# Revit family: svetilnik_alfresco_bourdon
name_source: partatom
category: Lighting Fixtures
revit_build: Autodesk Revit 2016 (Build: 20150506_1715(x64)
units: mm (PartAtom-declared; Revit-internal decimal feet)

## family parameters
Always vertical = Yes
Cut with Voids When Loaded = No
Light Source = Yes
Part Type = Normal
Room Calculation Point = No
Round Connector Dimension = Use Diameter
Shared = No
Work Plane-Based = No

## types (2) — shared parameters
ADSK_Единица измерения = шт.
ADSK_Завод-изготовитель = ALFRESCO
ADSK_Количество фаз = 2
ADSK_Количество фаз числовое = 2
ADSK_Коэффициент мощности = 0.98
ADSK_Масса = 36
ADSK_Напряжение = 220 V
ADSK_Номинальная мощность = 70 W
ADSK_Полная мощность = 71 VA
ADSK_Размер_Высота = 4175 mm  [stored 13.6975 ft]
ADSK_Размер_Диаметр = 300 mm
ADSK_Размер_Длина = 652 mm  [stored 2.13911 ft]
ADSK_Ток = 0 A
ADSK_Энергоэффективность = 90 lm/W
Apparent Load = 71 VA
Color Filter = 16777215
Dimming Lamp Color Temperature Shift = <None>
Emit from Line Length = 80 mm  [stored 0.262467 ft]
IP Class = IP 54
Manufacturer = ALFRESCO
Photometric Web File = Боурдон_70Вт_ДНаТ.ies
Tilt Angle = 90.00°
URL = http://www.allfresco.ru
Блок аварийного питания = No
Класс защиты = 1
Класс пожароопасности = F (светильники предназначены для установки непосредственно на поверхность из нормально воспламеняемых материалов)
Климатическая зона = УХЛ1
Корпус светильника = Антрацит
Материал рассеивателя = РС
Область использования = ландшафт, коттедж. Посёлки,микрорайоны,АЗС, автостоянки
Отражатель = Отражатель
Рассеиватель = Стекло светильника
Световой поток2 = 6300 lm
Температура эксплуатации = -30 +40
Тип ИС = ДнаТ лампа
Тип КСС = Круглосимметричная
Тип ПРА = -
Тип продукции = Комплект(Опора освещения+ плафон+арматура)
Цветовая температура = 2700
Цоколь = Антрацит

## per-type parameters (varying)
| type | ADSK_Артикул | ADSK_Наименование | Плафон 1 | Плафон 2 |
| Боурдон1 | 1105001031 | Боурдон1 ДНаТ 70 - плафон Баллон B4 /05 прозр. с 2-мя лепестками на опоре ОССв 3,6 ЧС | Yes | No |
| Боурдон2 | 1105001011 | Боурдон2 ДнаТ 70 - плафон Конус B3 /05 прозр. матированный с 2-мя лепестками на опоре ОССв 3,6 ЧС | No | Yes |

note: column(s) folded — value = type name in every type: ADSK_Модель

note: [stored X ft] marks values corroborated as IEEE doubles in the binary element streams (Revit-internal decimal feet)

## geometry (parser evidence)
native form markers: Blend x2
no freeform markers — native parametric forms only
